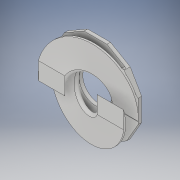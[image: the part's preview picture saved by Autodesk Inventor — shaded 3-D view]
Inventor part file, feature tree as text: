
AUTODESK INVENTOR PART (.ipt)
format: ipt  version: 2017 (Build 210142000, 142)  size: 384,000 bytes
history: native  units: in
note: dims shown in document units (in); Inventor stores cm internally (conversion verified against a paired STEP export)
features: fillet x2, extrude x1, helix x1, sketch x1
ambient origin geometry x8: Origin, YZ Plane, XZ Plane, XY Plane, X Axis, Y Axis, Z Axis, Center Point
bodies: Solid1 (feature_tree)
feature tree (5):
  extrude  "Extrusion1"  Depth=0.125in TaperAngle=0.0deg
  helix  "Coil1"  [1 undecoded]
  fillet  "Fillet1"  Radius=0.3in
  fillet  "Fillet2"  Radius=0.3in
  sketch  "Sketch2"  dims[d0=1.125in d2=0.125in d3=0.0in d4=2.95in d5=0.3in d6=0.3in d7=0.3in d8=0.3in d9=1.0in d10=0.5in d11=0.1969in d12=0.0in d13=90.0deg d14=90.0deg d15=0.0in d16=0.0in d17=0.125in d18=0.05in]
note: 1 required parameter value undecoded (feature->parameter linkage not recoverable at this tier; creation-order binding heuristic only, values carry confidence <= 0.55)
